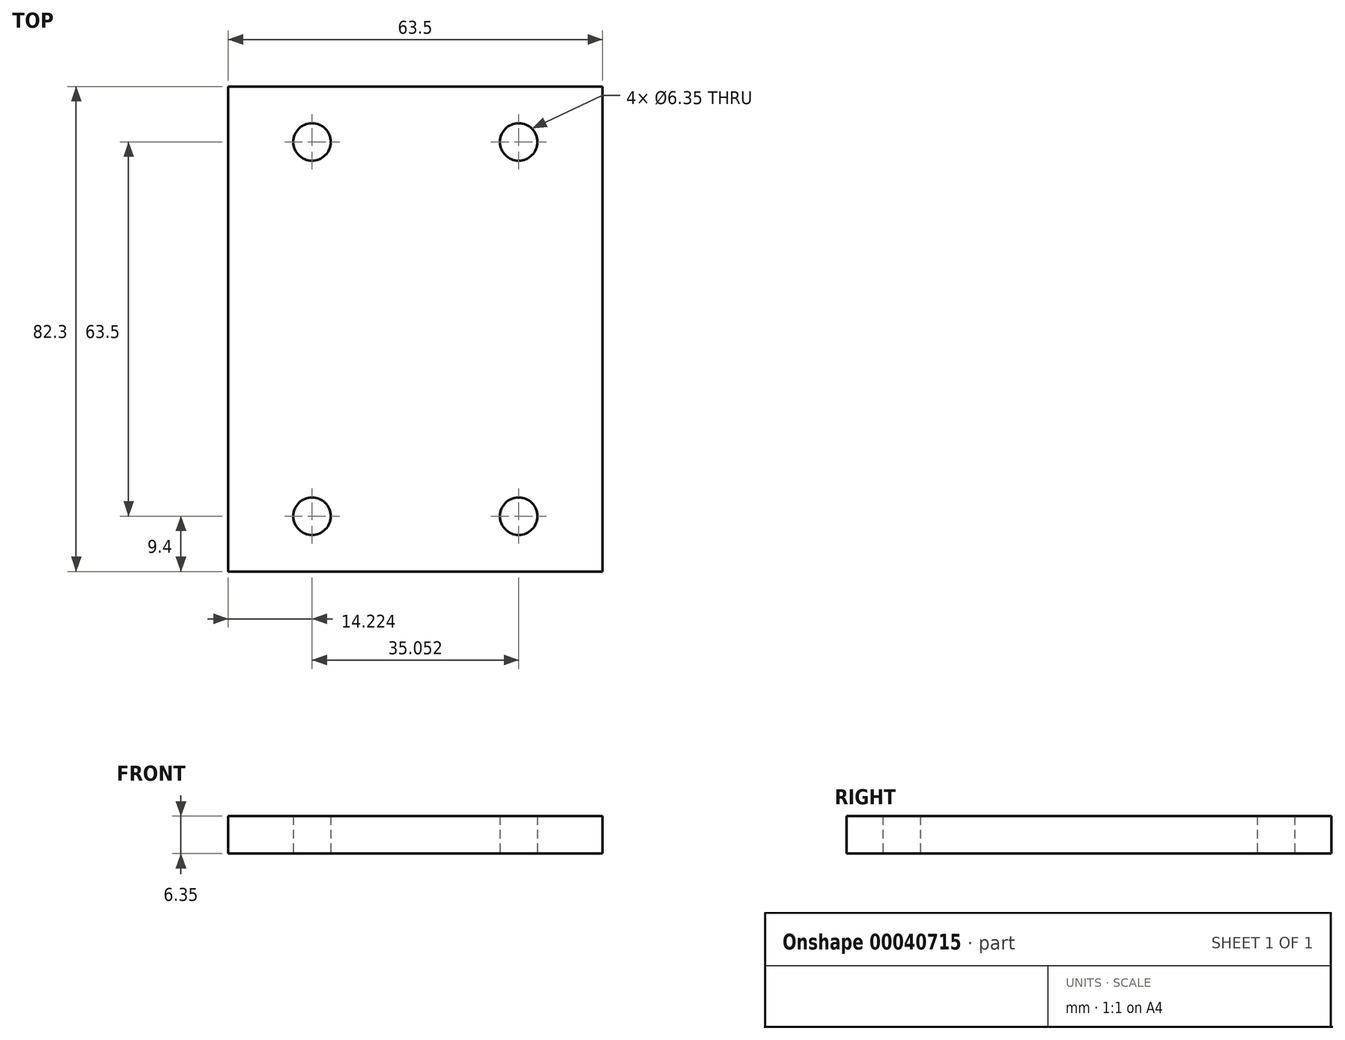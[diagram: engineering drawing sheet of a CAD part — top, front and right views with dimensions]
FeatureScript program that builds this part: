
annotation { "Feature Type Name" : "Feature", "Feature Type Description" : "" }
export const myFeature = defineFeature(function(context is Context, id is Id, definition is map)
    precondition{}
    {
        {
            var Q0;
            Q0=qCreatedBy(makeId("Top.planeOp"),FACE);
            var sketch = newSketch(context, id + "F0", { "sketchPlane" : qUnion([Q0])});
            skLineSegment(sketch, "E0.rect.bottom", {"start": v(-31.75, 41.15) * mm, "end": v(31.75, 41.15) * mm});
            skLineSegment(sketch, "E0.rect.top", {"start": v(-31.75, -41.15) * mm, "end": v(31.75, -41.15) * mm});
            skLineSegment(sketch, "E0.rect.left", {"start": v(-31.75, 41.15) * mm, "end": v(-31.75, -41.15) * mm});
            skLineSegment(sketch, "E0.rect.right", {"start": v(31.75, 41.15) * mm, "end": v(31.75, -41.15) * mm});
            skPoint(sketch, "E0.rect.middle", {"position": v(0, 0) * mm});
            skLineSegment(sketch, "E1", {"start": v(31.75, 0) * mm, "end": v(-31.75, 0) * mm, "construction": true});
            skLineSegment(sketch, "E2", {"start": v(0, 41.15) * mm, "end": v(0, -41.15) * mm, "construction": true});
            skLineSegment(sketch, "E3.0", {"start": v(31.75, -31.75) * mm, "end": v(-31.75, -31.75) * mm, "construction": true});
            skLineSegment(sketch, "E4.0", {"start": v(-17.53, 41.15) * mm, "end": v(-17.53, -41.15) * mm, "construction": true});
            skCircle(sketch, "E5", {"center": v(-17.53, -31.75) * mm, "radius": 3.18 * mm});
            skCircle(sketch, "E6.MirrorC", {"center": v(17.53, -31.75) * mm, "radius": 3.18 * mm});
            skCircle(sketch, "E7.MirrorC", {"center": v(-17.53, 31.75) * mm, "radius": 3.18 * mm});
            skCircle(sketch, "E8.MirrorC", {"center": v(17.53, 31.75) * mm, "radius": 3.18 * mm});
            skSolve(sketch);
        }
        {
            var Q0;
            Q0 = qSketchRegion(id + "F0", true);
            extrude(context, id + "F1", {"entities" : qUnion([Q0]), "depth" : 6.35 * mm});
        }
    });
